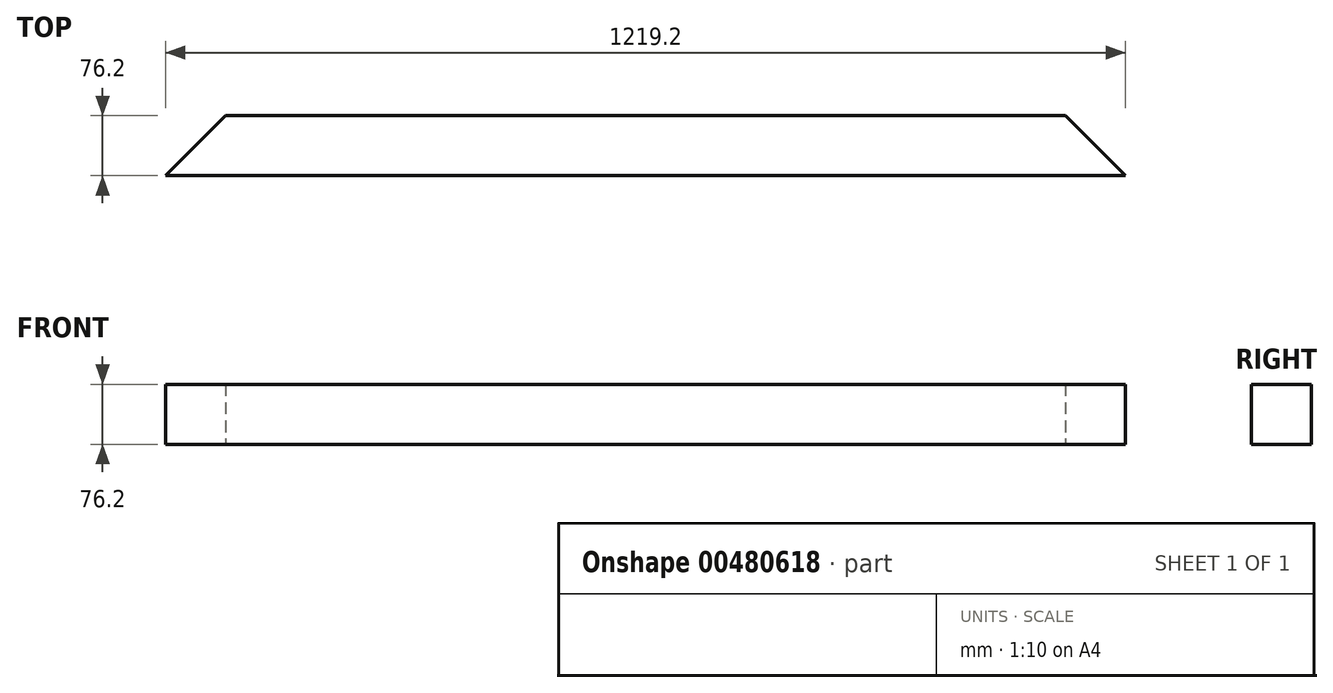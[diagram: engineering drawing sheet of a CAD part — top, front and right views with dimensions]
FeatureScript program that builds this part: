
annotation { "Feature Type Name" : "Feature", "Feature Type Description" : "" }
export const myFeature = defineFeature(function(context is Context, id is Id, definition is map)
    precondition{}
    {
        {
            var Q0;
            Q0=qCreatedBy(makeId("Top.planeOp"),FACE);
            var sketch = newSketch(context, id + "F0", { "sketchPlane" : qUnion([Q0])});
            skLineSegment(sketch, "E0.bottom", {"start": v(603, 38.1) * mm, "end": v(-463.8, 38.1) * mm});
            skLineSegment(sketch, "E0.top", {"start": v(679.2, -38.1) * mm, "end": v(-540, -38.1) * mm});
            skPoint(sketch, "E0.middle", {"position": v(69.6, 0) * mm});
            skLineSegment(sketch, "E1", {"start": v(-540, -38.1) * mm, "end": v(-463.8, 38.1) * mm});
            skLineSegment(sketch, "E2", {"start": v(679.2, -38.1) * mm, "end": v(603, 38.1) * mm});
            skPoint(sketch, "E0.right.start.orphan", {"position": v(-540, 38.1) * mm});
            skPoint(sketch, "E0.left.start.orphan", {"position": v(679.2, 38.1) * mm});
            skSolve(sketch);
        }
        {
            var Q0;
            Q0 = qSketchRegion(id + "F0", true);
            extrude(context, id + "F1", {"entities" : qUnion([Q0]), "depth" : 76.2 * mm});
        }
    });
